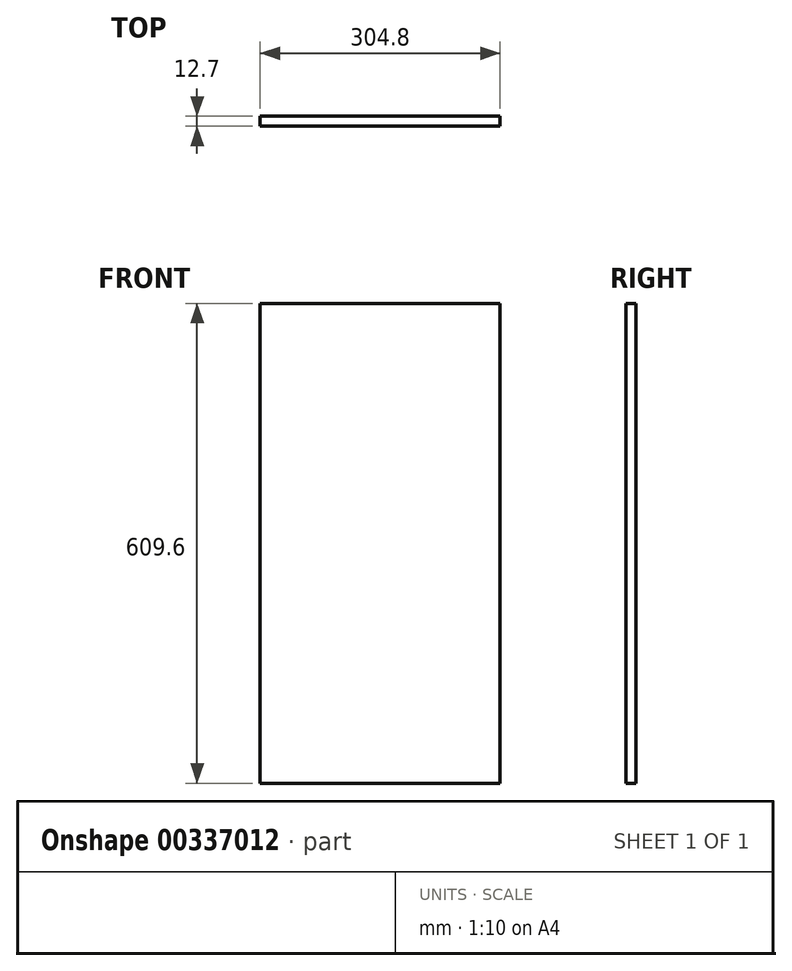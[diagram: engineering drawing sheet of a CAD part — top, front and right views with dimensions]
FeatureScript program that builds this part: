
annotation { "Feature Type Name" : "Feature", "Feature Type Description" : "" }
export const myFeature = defineFeature(function(context is Context, id is Id, definition is map)
    precondition{}
    {
        {
            var Q0;
            Q0=qCreatedBy(makeId("Front.planeOp"),FACE);
            var sketch = newSketch(context, id + "F0", { "sketchPlane" : qUnion([Q0])});
            skLineSegment(sketch, "E0.bottom", {"start": v(-150.2, 469.22) * mm, "end": v(154.6, 469.22) * mm});
            skLineSegment(sketch, "E0.top", {"start": v(-150.2, -140.38) * mm, "end": v(154.6, -140.38) * mm});
            skLineSegment(sketch, "E0.left", {"start": v(-150.2, 469.22) * mm, "end": v(-150.2, -140.38) * mm});
            skLineSegment(sketch, "E0.right", {"start": v(154.6, 469.22) * mm, "end": v(154.6, -140.38) * mm});
            skSolve(sketch);
        }
        {
            var Q0;
            Q0 = qSketchRegion(id + "F0", true);
            extrude(context, id + "F1", {"entities" : qUnion([Q0]), "depth" : 12.7 * mm});
        }
    });
